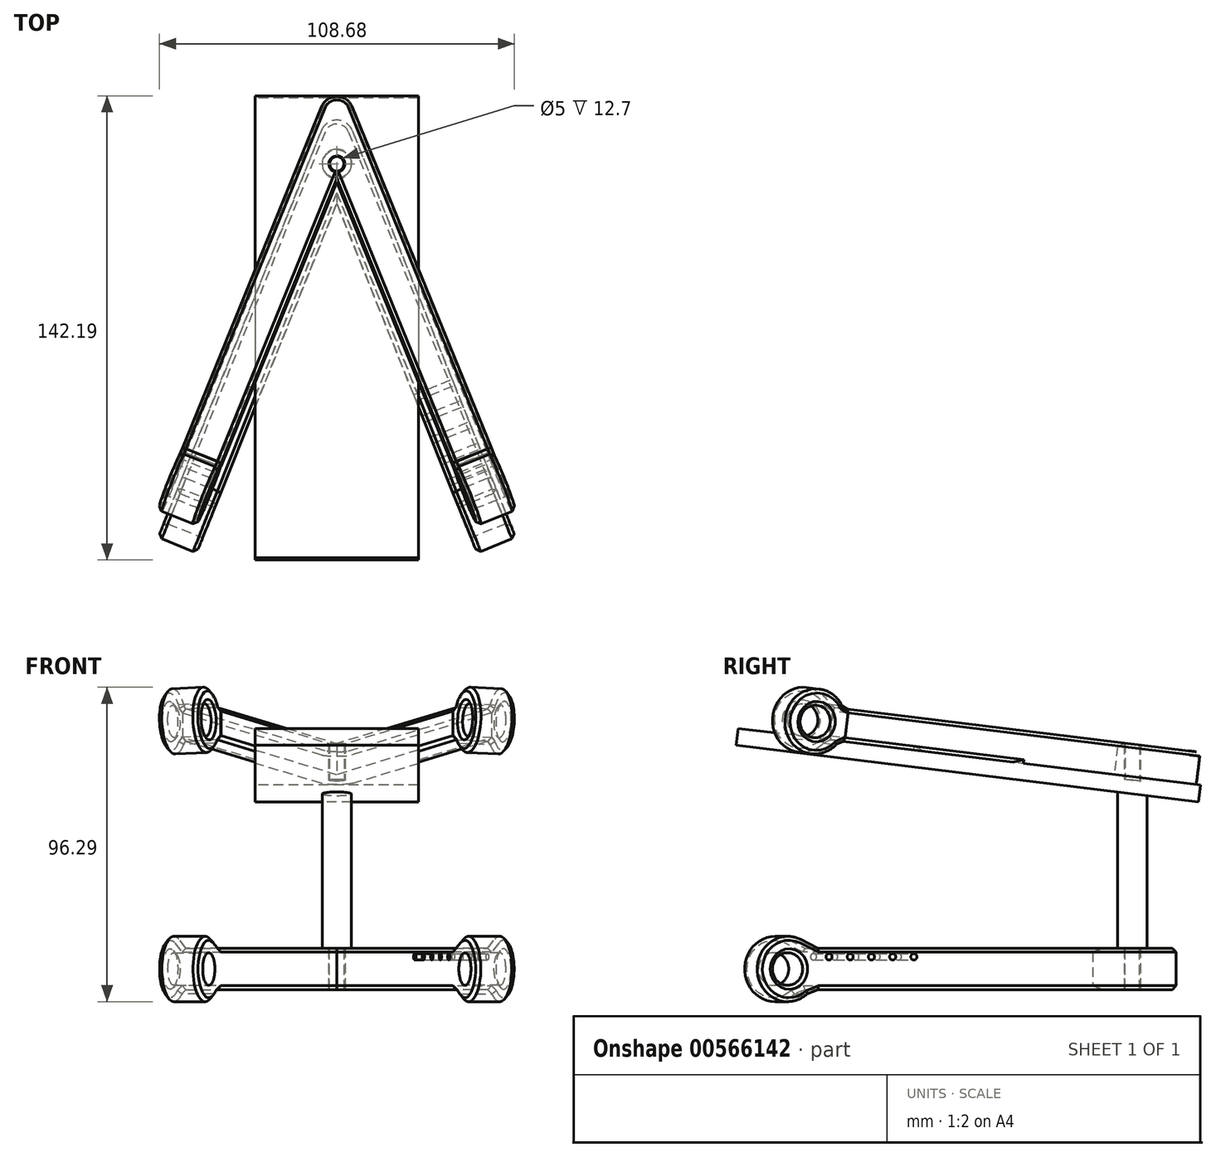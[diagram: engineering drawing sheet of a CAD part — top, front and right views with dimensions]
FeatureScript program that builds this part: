
annotation { "Feature Type Name" : "Feature", "Feature Type Description" : "" }
export const myFeature = defineFeature(function(context is Context, id is Id, definition is map)
    precondition{}
    {
        {
            var Q0;
            Q0=qCreatedBy(makeId("Top.planeOp"),FACE);
            var sketch = newSketch(context, id + "F0", { "sketchPlane" : qUnion([Q0])});
            skLineSegment(sketch, "E0", {"start": v(-47.3, -49.5) * mm, "end": v(0, 68.36) * mm});
            skLineSegment(sketch, "E1", {"start": v(0, 68.36) * mm, "end": v(47.3, -49.5) * mm});
            skLineSegment(sketch, "E2.0", {"start": v(0, 34.26) * mm, "end": v(35.5, -54.23) * mm});
            skLineSegment(sketch, "E2.1", {"start": v(-35.5, -54.23) * mm, "end": v(0, 34.26) * mm});
            skLineSegment(sketch, "E3", {"start": v(-47.3, -49.5) * mm, "end": v(-35.5, -54.23) * mm});
            skLineSegment(sketch, "E4", {"start": v(35.5, -54.23) * mm, "end": v(47.3, -49.5) * mm});
            skLineSegment(sketch, "E5", {"start": v(0, 34.26) * mm, "end": v(0, 68.36) * mm, "construction": true});
            skCircle(sketch, "E6", {"center": v(0, 46.36) * mm, "radius": 2.5 * mm});
            skSolve(sketch);
        }
        {
            var Q0;
            Q0=makeQuery(id+"F0.imprint","IMPRINT",FACE,{"disambiguationData":[TD([[makeQuery(id+"F0.imprint","IMPRINT",EDGE,{"derivedFrom":sQuery(id+"F0.wireOp",EDGE,"E0")}),-1.0]])]});
            extrude(context, id + "F1", {"entities" : qUnion([Q0]), "depth" : 12.7 * mm, "offsetDistance" : 25.4 * mm});
        }
        {
            var Q0;
            Q0=makeQuery(id+"F1.opExtrude","SWEPT_EDGE",EDGE,{"disambiguationData":[OSD([sQuery(id+"F0.wireOp",EDGE,"E0"),sQuery(id+"F0.wireOp",EDGE,"E1")])]});
            fillet(context, id + "F2", {"entities" : qUnion([Q0]), "radius" : 5.08 * mm, "tangentPropagation" : true, "allowEdgeOverflow" : false});
        }
        {
            var Q0;
            Q0=makeQuery(id+"F1.opExtrude","SWEPT_FACE",FACE,{"disambiguationData":[OSD([sQuery(id+"F0.wireOp",EDGE,"E0")])]});
            var sketch = newSketch(context, id + "F3", { "sketchPlane" : qUnion([Q0])});
            skArc(sketch, "E7", {"start": v(67.11, -1.3) * mm, "mid": v(83.47, 5.03) * mm, "end": v(69.34, 15.42) * mm});
            skLineSegment(sketch, "E8", {"start": v(-50.78, 6.35) * mm, "end": v(102.72, 6.35) * mm, "construction": true});
            skPoint(sketch, "E8.endSnap0", {"position": v(63.56, 6.35) * mm});
            skLineSegment(sketch, "E9", {"start": v(63.56, 0) * mm, "end": v(67.11, -1.3) * mm});
            skPoint(sketch, "E10.orphan", {"position": v(73.56, 16.35) * mm});
            skPoint(sketch, "E11.orphan", {"position": v(73.56, -3.65) * mm});
            skLineSegment(sketch, "E12", {"start": v(63.56, 12.7) * mm, "end": v(69.34, 15.42) * mm});
            skSolve(sketch);
        }
        {
            var Q0;
            Q0=makeQuery(id+"F3.imprint","IMPRINT",FACE,{"disambiguationData":[TD([[makeQuery(id+"F3.imprint","IMPRINT",EDGE,{"derivedFrom":sQuery(id+"F3.wireOp",EDGE,"E7")}),1.0]])]});
            var Q1;
            Q1=makeQuery(id+"F1.opExtrude","SWEPT_FACE",FACE,{"disambiguationData":[OSD([sQuery(id+"F0.wireOp",EDGE,"E2.1")])]});
            var Q2;
            Q2=makeQuery(id+"F1.opExtrude","SWEPT_FACE",FACE,{"disambiguationData":[OSD([sQuery(id+"F0.wireOp",EDGE,"E2.1")])]});
            extrude(context, id + "F4", {"entities" : qUnion([Q0]), "operationType" : NewBodyOperationType.ADD, "endBound" : BoundingType.UP_TO_SURFACE, "oppositeDirection" : true, "depth" : 4.6 * mm, "endBoundEntityFace" : qUnion([Q1]), "offsetDistance" : 25 * mm});
        }
        {
            var Q0;
            Q0=makeQuery(id+"F4.boolean.opBoolean","MERGE",FACE,{"derivedFrom":[makeQuery(id+"F1.opExtrude","SWEPT_FACE",FACE,{"disambiguationData":[OSD([sQuery(id+"F0.wireOp",EDGE,"E2.1")])]}),makeQuery(id+"F4.opExtrude","CAP_FACE",FACE,{"disambiguationData":[OSD([sQuery(id+"F0.wireOp",EDGE,"E0"),sQuery(id+"F0.wireOp",EDGE,"E3"),sQuery(id+"F3.wireOp",EDGE,"E7"),sQuery(id+"F3.wireOp",EDGE,"E9"),sQuery(id+"F3.wireOp",EDGE,"E12")])],"isStart":false})]});
            var sketch = newSketch(context, id + "F5", { "sketchPlane" : qUnion([Q0])});
            skLineSegment(sketch, "E13", {"start": v(-63.56, 0) * mm, "end": v(-63.56, 12.7) * mm, "construction": true});
            skLineSegment(sketch, "E14", {"start": v(-63.56, 12.7) * mm, "end": v(-63.56, 6.35) * mm, "construction": true});
            skLineSegment(sketch, "E15", {"start": v(-63.56, 6.35) * mm, "end": v(-83.56, 6.35) * mm, "construction": true});
            skCircle(sketch, "E16", {"center": v(-73.56, 6.35) * mm, "radius": 5 * mm});
            skSolve(sketch);
        }
        {
            var Q0;
            Q0=makeQuery(id+"F5.imprint","IMPRINT",FACE,{"disambiguationData":[TD([[makeQuery(id+"F5.imprint","IMPRINT",EDGE,{"derivedFrom":sQuery(id+"F5.wireOp",EDGE,"E16")}),1.0]])]});
            extrude(context, id + "F6", {"entities" : qUnion([Q0]), "operationType" : NewBodyOperationType.REMOVE, "oppositeDirection" : true, "depth" : 25 * mm, "offsetDistance" : 25 * mm});
        }
        {
            var Q0;
            Q0=makeQuery(id+"F1.opExtrude","CAP_FACE",FACE,{"disambiguationData":[OSD([sQuery(id+"F0.wireOp",EDGE,"E0"),sQuery(id+"F0.wireOp",EDGE,"E1"),sQuery(id+"F0.wireOp",EDGE,"E2.0"),sQuery(id+"F0.wireOp",EDGE,"E2.1"),sQuery(id+"F0.wireOp",EDGE,"E3"),sQuery(id+"F0.wireOp",EDGE,"E4"),sQuery(id+"F0.wireOp",EDGE,"E6")])],"isStart":false});
            var sketch = newSketch(context, id + "F7", { "sketchPlane" : qUnion([Q0])});
            skCircle(sketch, "E17", {"center": v(0, 46.36) * mm, "radius": 2.25 * mm});
            skSolve(sketch);
        }
        {
            var Q0;
            Q0=makeQuery(id+"F7.imprint","IMPRINT",FACE,{"disambiguationData":[TD([[makeQuery(id+"F7.imprint","IMPRINT",EDGE,{"derivedFrom":sQuery(id+"F7.wireOp",EDGE,"E17")}),1.0]])]});
            var Q1;
            Q1=makeQuery(id+"F1.opExtrude","CAP_FACE",FACE,{"disambiguationData":[OSD([sQuery(id+"F0.wireOp",EDGE,"E0"),sQuery(id+"F0.wireOp",EDGE,"E1"),sQuery(id+"F0.wireOp",EDGE,"E2.0"),sQuery(id+"F0.wireOp",EDGE,"E2.1"),sQuery(id+"F0.wireOp",EDGE,"E3"),sQuery(id+"F0.wireOp",EDGE,"E4"),sQuery(id+"F0.wireOp",EDGE,"E6")])],"isStart":true});
            extrude(context, id + "F8", {"entities" : qUnion([Q0]), "endBound" : BoundingType.UP_TO_SURFACE, "oppositeDirection" : true, "depth" : 16 * mm, "endBoundEntityFace" : qUnion([Q1]), "offsetDistance" : 25 * mm});
        }
        {
            var Q0;
            Q0=makeQuery(id+"F8.opExtrude","CAP_FACE",FACE,{"disambiguationData":[OSD([sQuery(id+"F7.wireOp",EDGE,"E17")])],"isStart":true});
            var sketch = newSketch(context, id + "F9", { "sketchPlane" : qUnion([Q0])});
            skCircle(sketch, "E18", {"center": v(0, 46.36) * mm, "radius": 4.5 * mm});
            skSolve(sketch);
        }
        {
            var Q0;
            Q0=makeQuery(id+"F9.imprint","IMPRINT",FACE,{"disambiguationData":[TD([[makeQuery(id+"F9.imprint","IMPRINT",EDGE,{"derivedFrom":sQuery(id+"F9.wireOp",EDGE,"E18")}),1.0]])]});
            var Q1;
            Q1=makeQuery(id+"F9.imprint","IMPRINT",FACE,{"disambiguationData":[TD([[makeQuery(id+"F9.imprint","IMPRINT",EDGE,{"derivedFrom":makeQuery(id+"F8.opExtrude","CAP_EDGE",EDGE,{"disambiguationData":[OSD([sQuery(id+"F7.wireOp",EDGE,"E17")])],"isStart":true})}),1.0]])]});
            extrude(context, id + "F10", {"entities" : qUnion([Q0, Q1]), "operationType" : NewBodyOperationType.ADD, "depth" : 50 * mm, "offsetDistance" : 25 * mm});
        }
        {
            var Q0;
            Q0=qCreatedBy(makeId("Right.planeOp"),FACE);
            var sketch = newSketch(context, id + "F11", { "sketchPlane" : qUnion([Q0])});
            skLineSegment(sketch, "E19.bottom", {"start": v(-75.3, 47.45) * mm, "end": v(67.82, 47.45) * mm});
            skLineSegment(sketch, "E19.top", {"start": v(-75.3, -10.9) * mm, "end": v(67.82, -10.9) * mm});
            skLineSegment(sketch, "E19.left", {"start": v(-75.3, 47.45) * mm, "end": v(-75.3, -10.9) * mm});
            skLineSegment(sketch, "E19.right", {"start": v(67.82, 47.45) * mm, "end": v(67.82, -10.9) * mm});
            skSolve(sketch);
        }
        {
            var Q0;
            Q0=makeQuery(id+"F11.imprint","IMPRINT",FACE,{"disambiguationData":[TD([[makeQuery(id+"F11.imprint","IMPRINT",EDGE,{"derivedFrom":sQuery(id+"F11.wireOp",EDGE,"E19.bottom")}),-1.0]])]});
            var Q1;
            Q1=sQuery(id+"F11.wireOp",EDGE,"E19.top");
            extrude(context, id + "F12", {"entities" : qUnion([Q0]), "operationType" : NewBodyOperationType.REMOVE, "surfaceEntities" : qUnion([Q1]), "depth" : 60.3 * mm, "offsetDistance" : 25 * mm});
        }
        {
            var Q0;
            Q0=makeQuery(id+"F10.opExtrude","CAP_FACE",FACE,{"disambiguationData":[OSD([sQuery(id+"F9.wireOp",EDGE,"E18")])],"isStart":false});
            var sketch = newSketch(context, id + "F13", { "sketchPlane" : qUnion([Q0])});
            skCircle(sketch, "E20", {"center": v(0, 46.36) * mm, "radius": 2.25 * mm});
            skSolve(sketch);
        }
        {
            var Q0;
            Q0=makeQuery(id+"F13.imprint","IMPRINT",FACE,{"disambiguationData":[TD([[makeQuery(id+"F13.imprint","IMPRINT",EDGE,{"derivedFrom":sQuery(id+"F13.wireOp",EDGE,"E20")}),1.0]])]});
            extrude(context, id + "F14", {"entities" : qUnion([Q0]), "operationType" : NewBodyOperationType.ADD, "depth" : 25 * mm, "offsetDistance" : 25 * mm});
        }
        {
            var Q0;
            Q0=qCreatedBy(makeId("Right.planeOp"),FACE);
            var sketch = newSketch(context, id + "F15", { "sketchPlane" : qUnion([Q0])});
            skLineSegment(sketch, "E21.bottom", {"start": v(66.59, 57.54) * mm, "end": v(-74.97, 74.92) * mm});
            skLineSegment(sketch, "E21.top", {"start": v(67.22, 62.66) * mm, "end": v(-74.34, 80.04) * mm});
            skLineSegment(sketch, "E21.left", {"start": v(66.59, 57.54) * mm, "end": v(67.22, 62.66) * mm});
            skLineSegment(sketch, "E21.right", {"start": v(-74.97, 74.92) * mm, "end": v(-74.34, 80.04) * mm});
            skLineSegment(sketch, "E22.0", {"start": v(41.86, 62.7) * mm, "end": v(50.86, 62.7) * mm});
            skSolve(sketch);
        }
        {
            var Q0;
            Q0=makeQuery(id+"F15.imprint","IMPRINT",FACE,{"disambiguationData":[TD([[makeQuery(id+"F15.imprint","IMPRINT",EDGE,{"derivedFrom":sQuery(id+"F15.wireOp",EDGE,"E21.bottom")}),-1.0]])]});
            extrude(context, id + "F16", {"entities" : qUnion([Q0]), "depth" : 25 * mm, "offsetDistance" : 25 * mm});
        }
        {
            var Q0;
            Q0=makeQuery(id+"F16.opExtrude","SWEPT_FACE",FACE,{"disambiguationData":[OSD([sQuery(id+"F15.wireOp",EDGE,"E21.top")])]});
            var sketch = newSketch(context, id + "F17", { "sketchPlane" : qUnion([Q0])});
            skLineSegment(sketch, "E23.0.0", {"start": v(-35.5, -55.38) * mm, "end": v(0, 32.46) * mm});
            skLineSegment(sketch, "E23.0.1", {"start": v(0, 32.46) * mm, "end": v(35.5, -55.38) * mm});
            skLineSegment(sketch, "E23.0.2", {"start": v(35.5, -55.38) * mm, "end": v(47.3, -50.68) * mm});
            skLineSegment(sketch, "E23.0.3", {"start": v(47.3, -50.68) * mm, "end": v(4.71, 54.64) * mm});
            skEllipticalArc(sketch, "E23.0.4", {});
            skLineSegment(sketch, "E23.0.5", {"start": v(-4.71, 54.64) * mm, "end": v(-47.3, -50.68) * mm});
            skLineSegment(sketch, "E23.0.6", {"start": v(-47.3, -50.68) * mm, "end": v(-35.5, -55.38) * mm});
            const initialGuessF17  = {"E23.0.4": [0, 0.05276548921720173, -1, 0, 0.00508, 0.005042134450337917, 3.5231966964359085, 5.901581264333471]};
            skSetInitialGuess(sketch, initialGuessF17);
            skSolve(sketch);
        }
        {
            var Q0;
            {var subQ4=sQuery(id+"F17.wireOp",EDGE,"E23.0.0");Q0=makeQuery(id+"F17.imprint","IMPRINT",FACE,{"disambiguationData":[TD([[makeQuery(id+"F17.imprint","IMPRINT",EDGE,{"derivedFrom":subQ4}),1.0]])]});}
            extrude(context, id + "F18", {"entities" : qUnion([Q0]), "depth" : 10 * mm, "offsetDistance" : 25 * mm});
        }
        {
            var Q0;
            Q0=makeQuery(id+"F10.opExtrude","CAP_FACE",FACE,{"disambiguationData":[OSD([sQuery(id+"F9.wireOp",EDGE,"E18")])],"isStart":false});
            var sketch = newSketch(context, id + "F19", { "sketchPlane" : qUnion([Q0])});
            skCircle(sketch, "E24", {"center": v(0, 46.36) * mm, "radius": 2.5 * mm});
            skSolve(sketch);
        }
        {
            var Q0;
            Q0=makeQuery(id+"F19.imprint","IMPRINT",FACE,{"disambiguationData":[TD([[makeQuery(id+"F19.imprint","IMPRINT",EDGE,{"derivedFrom":makeQuery(id+"F14.opExtrude","CAP_EDGE",EDGE,{"disambiguationData":[OSD([sQuery(id+"F13.wireOp",EDGE,"E20")])],"isStart":true})}),1.0]])]});
            var Q1;
            Q1=makeQuery(id+"F19.imprint","IMPRINT",FACE,{"disambiguationData":[TD([[makeQuery(id+"F19.imprint","IMPRINT",EDGE,{"derivedFrom":sQuery(id+"F19.wireOp",EDGE,"E24")}),1.0]])]});
            extrude(context, id + "F20", {"entities" : qUnion([Q0, Q1]), "operationType" : NewBodyOperationType.REMOVE, "depth" : 25 * mm, "offsetDistance" : 25 * mm});
        }
        {
            var Q0;
            Q0=makeQuery(id+"F14.opExtrude","CAP_FACE",FACE,{"disambiguationData":[OSD([sQuery(id+"F13.wireOp",EDGE,"E20")])],"isStart":false});
            var Q1;
            {var subQ0=makeQuery(id+"F18.opExtrude","CAP_FACE",FACE,{"disambiguationData":[OSD([sQuery(id+"F15.wireOp",EDGE,"E21.top"),sQuery(id+"F17.wireOp",EDGE,"E23.0.0"),sQuery(id+"F17.wireOp",EDGE,"E23.0.4"),sQuery(id+"F17.wireOp",EDGE,"E23.0.5"),sQuery(id+"F17.wireOp",EDGE,"E23.0.6")])],"isStart":false});Q1=makeQuery(id+"F95WDTQFAS0JUpE_4.boolean.opBoolean","MERGE",FACE,{"derivedFrom":[subQ0,makeQuery(id+"F95WDTQFAS0JUpE_4.opPattern","COPY",FACE,{"derivedFrom":subQ0,"instanceName":"1"})]});}
            extrude(context, id + "F21", {"entities" : qUnion([Q0]), "operationType" : NewBodyOperationType.REMOVE, "endBound" : BoundingType.UP_TO_SURFACE, "oppositeDirection" : true, "depth" : 25 * mm, "endBoundEntityFace" : qUnion([Q1]), "offsetDistance" : 25 * mm});
        }
        {
            var Q0;
            Q0=makeQuery(id+"F18.opExtrude","SWEPT_FACE",FACE,{"disambiguationData":[OSD([sQuery(id+"F17.wireOp",EDGE,"E23.0.5")])]});
            var sketch = newSketch(context, id + "F22", { "sketchPlane" : qUnion([Q0])});
            skArc(sketch, "E25", {"start": v(57.24, 77.34) * mm, "mid": v(74.04, 86.12) * mm, "end": v(55.34, 89.23) * mm});
            skLineSegment(sketch, "E26", {"start": v(-58.37, 68.31) * mm, "end": v(54.26, 83.23) * mm, "construction": true});
            skPoint(sketch, "E27.orphan", {"position": v(64.17, 94.54) * mm});
            skPoint(sketch, "E28.orphan", {"position": v(64.17, 74.54) * mm});
            skCircle(sketch, "E29", {"center": v(64.17, 84.54) * mm, "radius": 5 * mm});
            skLineSegment(sketch, "E30", {"start": v(53.6, 88.19) * mm, "end": v(55.34, 89.23) * mm});
            skLineSegment(sketch, "E31", {"start": v(54.91, 78.27) * mm, "end": v(57.24, 77.34) * mm});
            skSolve(sketch);
        }
        {
            var Q0;
            Q0=makeQuery(id+"F22.imprint","IMPRINT",FACE,{"disambiguationData":[TD([[makeQuery(id+"F22.imprint","IMPRINT",EDGE,{"derivedFrom":sQuery(id+"F22.wireOp",EDGE,"E25")}),1.0]])]});
            var Q1;
            Q1=makeQuery(id+"F18.opExtrude","SWEPT_FACE",FACE,{"disambiguationData":[OSD([sQuery(id+"F17.wireOp",EDGE,"E23.0.0")])]});
            extrude(context, id + "F23", {"entities" : qUnion([Q0]), "operationType" : NewBodyOperationType.ADD, "endBound" : BoundingType.UP_TO_SURFACE, "oppositeDirection" : true, "depth" : 25 * mm, "endBoundEntityFace" : qUnion([Q1]), "offsetDistance" : 25 * mm});
        }
        {
            var Q0;
            Q0=makeQuery(id+"F10.opExtrude","CAP_FACE",FACE,{"disambiguationData":[OSD([sQuery(id+"F9.wireOp",EDGE,"E18")])],"isStart":false});
            var Q1;
            {var subQ0=makeQuery(id+"F18.opExtrude","CAP_FACE",FACE,{"disambiguationData":[OSD([sQuery(id+"F15.wireOp",EDGE,"E21.top"),sQuery(id+"F17.wireOp",EDGE,"E23.0.0"),sQuery(id+"F17.wireOp",EDGE,"E23.0.4"),sQuery(id+"F17.wireOp",EDGE,"E23.0.5"),sQuery(id+"F17.wireOp",EDGE,"E23.0.6")])],"isStart":true});Q1=makeQuery(id+"F95WDTQFAS0JUpE_4.boolean.opBoolean","MERGE",FACE,{"derivedFrom":[subQ0,makeQuery(id+"F95WDTQFAS0JUpE_4.opPattern","COPY",FACE,{"derivedFrom":subQ0,"instanceName":"1"})]});}
            extrude(context, id + "F24", {"entities" : qUnion([Q0]), "operationType" : NewBodyOperationType.ADD, "endBound" : BoundingType.UP_TO_SURFACE, "depth" : 25 * mm, "endBoundEntityFace" : qUnion([Q1]), "hasOffset" : true, "offsetDistance" : 1 * mm});
        }
        {
            var Q0;
            Q0=makeQuery(id+"F1.opExtrude","CAP_EDGE",EDGE,{"disambiguationData":[OSD([sQuery(id+"F0.wireOp",EDGE,"E0")])],"isStart":false});
            var Q1;
            Q1=makeQuery(id+"F1.opExtrude","CAP_EDGE",EDGE,{"disambiguationData":[OSD([sQuery(id+"F0.wireOp",EDGE,"E0")])],"isStart":true});
            var Q2;
            Q2=makeQuery(id+"F4.opExtrude","CAP_EDGE",EDGE,{"disambiguationData":[OSD([sQuery(id+"F3.wireOp",EDGE,"E12")])],"isStart":true});
            var Q3;
            Q3=makeQuery(id+"F4.opExtrude","CAP_EDGE",EDGE,{"disambiguationData":[OSD([sQuery(id+"F3.wireOp",EDGE,"E7")])],"isStart":true});
            var Q4;
            Q4=makeQuery(id+"F4.opExtrude","CAP_EDGE",EDGE,{"disambiguationData":[OSD([sQuery(id+"F3.wireOp",EDGE,"E9")])],"isStart":true});
            var Q5;
            Q5=makeQuery(id+"F1.opExtrude","CAP_EDGE",EDGE,{"disambiguationData":[OSD([sQuery(id+"F0.wireOp",EDGE,"E2.1")])],"isStart":false});
            var Q6;
            Q6=makeQuery(id+"F1.opExtrude","CAP_EDGE",EDGE,{"disambiguationData":[OSD([sQuery(id+"F0.wireOp",EDGE,"E2.1")])],"isStart":true});
            var Q7;
            Q7=makeQuery(id+"F4.opExtrude","CAP_EDGE",EDGE,{"disambiguationData":[OSD([sQuery(id+"F3.wireOp",EDGE,"E7")])],"isStart":false});
            var Q8;
            Q8=makeQuery(id+"F4.opExtrude","CAP_EDGE",EDGE,{"disambiguationData":[OSD([sQuery(id+"F3.wireOp",EDGE,"E9")])],"isStart":false});
            var Q9;
            Q9=makeQuery(id+"F4.opExtrude","CAP_EDGE",EDGE,{"disambiguationData":[OSD([sQuery(id+"F3.wireOp",EDGE,"E12")])],"isStart":false});
            var Q10;
            Q10=makeQuery(id+"F6.boolean.opBoolean","COPY",EDGE,{"derivedFrom":makeQuery(id+"F6.opExtrude","CAP_EDGE",EDGE,{"disambiguationData":[OSD([sQuery(id+"F5.wireOp",EDGE,"E16")])],"isStart":true})});
            var Q11;
            {var subQ0=sQuery(id+"F0.wireOp",EDGE,"E0");Q11=makeQuery(id+"F6.boolean.opBoolean","INTERSECT",EDGE,{"derivedFrom":[makeQuery(id+"F4.boolean.opBoolean","MERGE",FACE,{"derivedFrom":[makeQuery(id+"F1.opExtrude","SWEPT_FACE",FACE,{"disambiguationData":[OSD([subQ0])]}),makeQuery(id+"F4.opExtrude","CAP_FACE",FACE,{"disambiguationData":[OSD([subQ0,sQuery(id+"F0.wireOp",EDGE,"E3"),sQuery(id+"F3.wireOp",EDGE,"E7"),sQuery(id+"F3.wireOp",EDGE,"E9"),sQuery(id+"F3.wireOp",EDGE,"E12")])],"isStart":true})]}),makeQuery(id+"F6.opExtrude","SWEPT_FACE",FACE,{"disambiguationData":[OSD([sQuery(id+"F5.wireOp",EDGE,"E16")])]})]});}
            chamfer(context, id + "F25", {"entities" : qUnion([Q0, Q1, Q2, Q3, Q4, Q5, Q6, Q7, Q8, Q9, Q10, Q11]), "width" : 1.2 * mm, "tangentPropagation" : true});
        }
        {
            var Q0;
            Q0=makeQuery(id+"F1.opExtrude","SWEPT_BODY",BODY,{"disambiguationData":[OSD([sQuery(id+"F0.wireOp",EDGE,"E0"),sQuery(id+"F0.wireOp",EDGE,"E1"),sQuery(id+"F0.wireOp",EDGE,"E2.0"),sQuery(id+"F0.wireOp",EDGE,"E2.1"),sQuery(id+"F0.wireOp",EDGE,"E3"),sQuery(id+"F0.wireOp",EDGE,"E4"),sQuery(id+"F0.wireOp",EDGE,"E6")])]});
            var Q1;
            Q1=makeQuery(id+"F11.imprint","IMPRINT",FACE,{"disambiguationData":[TD([[makeQuery(id+"F11.imprint","IMPRINT",EDGE,{"derivedFrom":sQuery(id+"F11.wireOp",EDGE,"E19.bottom")}),-1.0]])]});
            mirror(context, id + "F26", {"operationType" : NewBodyOperationType.ADD, "entities" : qUnion([Q0]), "mirrorPlane" : qUnion([Q1])});
        }
        {
            var Q0;
            Q0=makeQuery(id+"F18.opExtrude","CAP_EDGE",EDGE,{"disambiguationData":[OSD([sQuery(id+"F17.wireOp",EDGE,"E23.0.5")])],"isStart":false});
            var Q1;
            Q1=makeQuery(id+"F18.opExtrude","CAP_EDGE",EDGE,{"disambiguationData":[OSD([sQuery(id+"F17.wireOp",EDGE,"E23.0.5")])],"isStart":true});
            var Q2;
            Q2=makeQuery(id+"F18.opExtrude","CAP_EDGE",EDGE,{"disambiguationData":[OSD([sQuery(id+"F17.wireOp",EDGE,"E23.0.0")])],"isStart":false});
            var Q3;
            Q3=makeQuery(id+"F18.opExtrude","CAP_EDGE",EDGE,{"disambiguationData":[OSD([sQuery(id+"F17.wireOp",EDGE,"E23.0.4")])],"isStart":false});
            var Q4;
            Q4=makeQuery(id+"F18.opExtrude","CAP_EDGE",EDGE,{"disambiguationData":[OSD([sQuery(id+"F17.wireOp",EDGE,"E23.0.4")])],"isStart":true});
            var Q5;
            Q5=makeQuery(id+"F18.opExtrude","CAP_EDGE",EDGE,{"disambiguationData":[OSD([sQuery(id+"F17.wireOp",EDGE,"E23.0.0")])],"isStart":true});
            chamfer(context, id + "F27", {"entities" : qUnion([Q0, Q1, Q2, Q3, Q4, Q5]), "width" : 1.2 * mm});
        }
        {
            var Q0;
            Q0=makeQuery(id+"F23.opExtrude","CAP_EDGE",EDGE,{"disambiguationData":[OSD([sQuery(id+"F22.wireOp",EDGE,"E25")])],"isStart":false});
            var Q1;
            Q1=makeQuery(id+"F23.opExtrude","CAP_EDGE",EDGE,{"disambiguationData":[OSD([sQuery(id+"F22.wireOp",EDGE,"E31")])],"isStart":false});
            var Q2;
            Q2=makeQuery(id+"F23.opExtrude","CAP_EDGE",EDGE,{"disambiguationData":[OSD([sQuery(id+"F22.wireOp",EDGE,"E30")])],"isStart":false});
            var Q3;
            Q3=makeQuery(id+"F23.opExtrude","CAP_EDGE",EDGE,{"disambiguationData":[OSD([sQuery(id+"F22.wireOp",EDGE,"E30")])],"isStart":true});
            var Q4;
            Q4=makeQuery(id+"F23.opExtrude","CAP_EDGE",EDGE,{"disambiguationData":[OSD([sQuery(id+"F22.wireOp",EDGE,"E25")])],"isStart":true});
            var Q5;
            Q5=makeQuery(id+"F23.opExtrude","CAP_EDGE",EDGE,{"disambiguationData":[OSD([sQuery(id+"F22.wireOp",EDGE,"E31")])],"isStart":true});
            chamfer(context, id + "F28", {"entities" : qUnion([Q0, Q1, Q2, Q3, Q4, Q5]), "width" : 1.2 * mm});
        }
        {
            var Q0;
            Q0=makeQuery(id+"F23.opExtrude","CAP_EDGE",EDGE,{"disambiguationData":[OSD([sQuery(id+"F22.wireOp",EDGE,"E29")])],"isStart":true});
            var Q1;
            Q1=makeQuery(id+"F23.opExtrude","CAP_EDGE",EDGE,{"disambiguationData":[OSD([sQuery(id+"F22.wireOp",EDGE,"E29")])],"isStart":false});
            chamfer(context, id + "F29", {"entities" : qUnion([Q0, Q1]), "width" : 1.2 * mm, "tangentPropagation" : true});
        }
        {
            var Q0;
            Q0=makeQuery(id+"F18.opExtrude","SWEPT_BODY",BODY,{"disambiguationData":[OSD([sQuery(id+"F15.wireOp",EDGE,"E21.top"),sQuery(id+"F17.wireOp",EDGE,"E23.0.0"),sQuery(id+"F17.wireOp",EDGE,"E23.0.4"),sQuery(id+"F17.wireOp",EDGE,"E23.0.5"),sQuery(id+"F17.wireOp",EDGE,"E23.0.6")])]});
            var Q1;
            Q1=makeQuery(id+"F23.opExtrude","SWEPT_BODY",BODY,{"disambiguationData":[OSD([sQuery(id+"F17.wireOp",EDGE,"E23.0.5"),sQuery(id+"F17.wireOp",EDGE,"E23.0.6"),sQuery(id+"F22.wireOp",EDGE,"E25"),sQuery(id+"F22.wireOp",EDGE,"E29"),sQuery(id+"F22.wireOp",EDGE,"E30"),sQuery(id+"F22.wireOp",EDGE,"E31")])]});
            var Q2;
            Q2=makeQuery(id+"F11.imprint","IMPRINT",FACE,{"disambiguationData":[TD([[makeQuery(id+"F11.imprint","IMPRINT",EDGE,{"derivedFrom":sQuery(id+"F11.wireOp",EDGE,"E19.bottom")}),-1.0]])]});
            mirror(context, id + "F30", {"operationType" : NewBodyOperationType.ADD, "entities" : qUnion([Q0, Q1]), "mirrorPlane" : qUnion([Q2])});
        }
        {
            var Q0;
            {var subQ0=sQuery(id+"F0.wireOp",EDGE,"E0");Q0=makeQuery(id+"F26.opPattern","COPY",FACE,{"derivedFrom":makeQuery(id+"F4.boolean.opBoolean","MERGE",FACE,{"derivedFrom":[makeQuery(id+"F1.opExtrude","SWEPT_FACE",FACE,{"disambiguationData":[OSD([subQ0])]}),makeQuery(id+"F4.opExtrude","CAP_FACE",FACE,{"disambiguationData":[OSD([subQ0,sQuery(id+"F0.wireOp",EDGE,"E3"),sQuery(id+"F3.wireOp",EDGE,"E7"),sQuery(id+"F3.wireOp",EDGE,"E9"),sQuery(id+"F3.wireOp",EDGE,"E12")])],"isStart":true})]}),"instanceName":"1"});}
            var sketch = newSketch(context, id + "F31", { "sketchPlane" : qUnion([Q0])});
            skCircle(sketch, "E32", {"center": v(-60.35, 10.1) * mm, "radius": 1 * mm});
            skCircle(sketch, "E33.1.0.0", {"center": v(-53.35, 10.1) * mm, "radius": 1 * mm});
            skCircle(sketch, "E33.2.0.0", {"center": v(-46.35, 10.1) * mm, "radius": 1 * mm});
            skCircle(sketch, "E33.3.0.0", {"center": v(-39.35, 10.1) * mm, "radius": 1 * mm});
            skCircle(sketch, "E33.4.0.0", {"center": v(-32.35, 10.1) * mm, "radius": 1 * mm});
            skLineSegment(sketch, "E33.direction1", {"start": v(-60.35, 10.1) * mm, "end": v(-53.35, 10.1) * mm, "construction": true});
            skSolve(sketch);
        }
        {
            var Q0;
            Q0=makeQuery(id+"F31.imprint","IMPRINT",FACE,{"disambiguationData":[TD([[makeQuery(id+"F31.imprint","IMPRINT",EDGE,{"derivedFrom":sQuery(id+"F31.wireOp",EDGE,"E32")}),1.0]])]});
            var Q1;
            Q1=makeQuery(id+"F31.imprint","IMPRINT",FACE,{"disambiguationData":[TD([[makeQuery(id+"F31.imprint","IMPRINT",EDGE,{"derivedFrom":sQuery(id+"F31.wireOp",EDGE,"E33.1.0.0")}),1.0]])]});
            var Q2;
            Q2=makeQuery(id+"F31.imprint","IMPRINT",FACE,{"disambiguationData":[TD([[makeQuery(id+"F31.imprint","IMPRINT",EDGE,{"derivedFrom":sQuery(id+"F31.wireOp",EDGE,"E33.2.0.0")}),1.0]])]});
            var Q3;
            Q3=makeQuery(id+"F31.imprint","IMPRINT",FACE,{"disambiguationData":[TD([[makeQuery(id+"F31.imprint","IMPRINT",EDGE,{"derivedFrom":sQuery(id+"F31.wireOp",EDGE,"E33.3.0.0")}),1.0]])]});
            var Q4;
            Q4=makeQuery(id+"F31.imprint","IMPRINT",FACE,{"disambiguationData":[TD([[makeQuery(id+"F31.imprint","IMPRINT",EDGE,{"derivedFrom":sQuery(id+"F31.wireOp",EDGE,"E33.4.0.0")}),1.0]])]});
            extrude(context, id + "F32", {"entities" : qUnion([Q0, Q1, Q2, Q3, Q4]), "operationType" : NewBodyOperationType.REMOVE, "oppositeDirection" : true, "depth" : 25 * mm, "offsetDistance" : 25 * mm});
        }
    });
